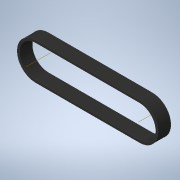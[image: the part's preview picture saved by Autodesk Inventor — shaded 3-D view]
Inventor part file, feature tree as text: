
AUTODESK INVENTOR PART (.ipt)
format: ipt  version: 2022.3 (Build 263350000, 350)  size: 177,664 bytes
history: native  units: in
note: dims shown in document units (in); Inventor stores cm internally (conversion verified against a paired STEP export)
features: sketch x4, extrude x1, other x1, projected_geometry x1
ambient origin geometry x8: Origin, YZ Plane, XZ Plane, XY Plane, X Axis, Y Axis, Z Axis, Center Point
bodies: Body1 (feature_tree)
feature tree (7):
  sketch  "Sketch1"  dims[d0=0.9023in d1=0.9023in]
  sketch  "Sketch2"  dims[d2=1.4174in]
  extrude  "Extrusion2"  Depth=0.9023in
  sketch  "Sketch5"  dims[d5=2.7165in d9=0.0787in d10=0.0598in d11=0.0299in d12=0.0219in d13=0.0219in d14=0.0059in d15=0.0059in d20=0.3346in d21=0.0in d22=0.0787in d23=0.0598in d24=0.0299in d25=0.0219in d26=0.0219in d27=0.0059in d28=0.0059in d29=0.0299in d30=0.0394in d31=0.0787in d32=0.0232in d34=0.0219in d35=0.0in d36=0.0in d37=0.0059in d38=0.0022in d39=0.0022in d40=0.0in d41=0.0in d42=0.0081in d43=0.0081in d44=0.0299in]
  other  "Work Axis1"
  sketch  "Sketch4"  dims[d3=1.4174in]
  projected_geometry  "Projected Loop1"
